# Revit family: ARKOSLIGHT_Black Foster micro 24V
name_source: partatom
category: Lighting Fixtures
units: mm (PartAtom-declared; Revit-internal decimal feet)

## family parameters
Cut with Voids When Loaded = No
Host = Face
Light Source = No
Part Type = Normal
Room Calculation Point = No
Round Connector Dimension = Use Diameter
Shared = No

## types (3) — shared parameters
ARKOSLIGHT_Apparent Load = 7 VA
ARKOSLIGHT_Beam Angle = 37.00°
ARKOSLIGHT_Body Color = ARKOSLIGHT_Matt black
ARKOSLIGHT_CRI = CRI>90
ARKOSLIGHT_Color = Matt black
ARKOSLIGHT_Dimming = No Dim
ARKOSLIGHT_Efficiency = 87%
ARKOSLIGHT_Fixture Type = TRACKLIGHTS
ARKOSLIGHT_IP = 20
ARKOSLIGHT_Lampshade_color = ARKOSLIGHT_Black
ARKOSLIGHT_Model = MINIMAL TRACK
ARKOSLIGHT_Series = BLACK FOSTER MICRO 24V
ARKOSLIGHT_Wattage = 8 W
Apparent Load = 7 VA
Description = Not valid for Minimal Track 24V Trimless
Manufacturer = ARKOSLIGHT
Model = MINIMAL TRACK
URL = https://www.arkoslight.com
zero-valued in all types: Default Elevation

## per-type parameters (varying)
| type | ARKOSLIGHT_CCT | ARKOSLIGHT_IES | ARKOSLIGHT_Luminous flux | ARKOSLIGHT_Reference | IES |
| A4152010N - BLACK FOSTER MICRO 24V 5 2700K N | 2700 K | A4152010 BLACK FOSTER MICRO 24V 5 2700K CRI90.ies | 775 lm | A4152010N | IES : A4152010N - BLACK FOSTER MICRO 24V 5 2700K N |
| A4152011N - BLACK FOSTER MICRO 24V 5 3000K N | 3000 K | A4152011 BLACK FOSTER MICRO 24V 5 3000K CRI90.ies | 800 lm | A4152011N | IES : A4152011N - BLACK FOSTER MICRO 24V 5 3000K N |
| A4152012N - BLACK FOSTER MICRO 24V 5 4000K N | 4000 K | A4152012 BLACK FOSTER MICRO 24V 5 4000K CRI90.ies | 850 lm | A4152012N | IES : A4152012N - BLACK FOSTER MICRO 24V 5 4000K N |

## geometry (parser evidence)
native form markers: Sweep x6
no freeform markers — native parametric forms only
